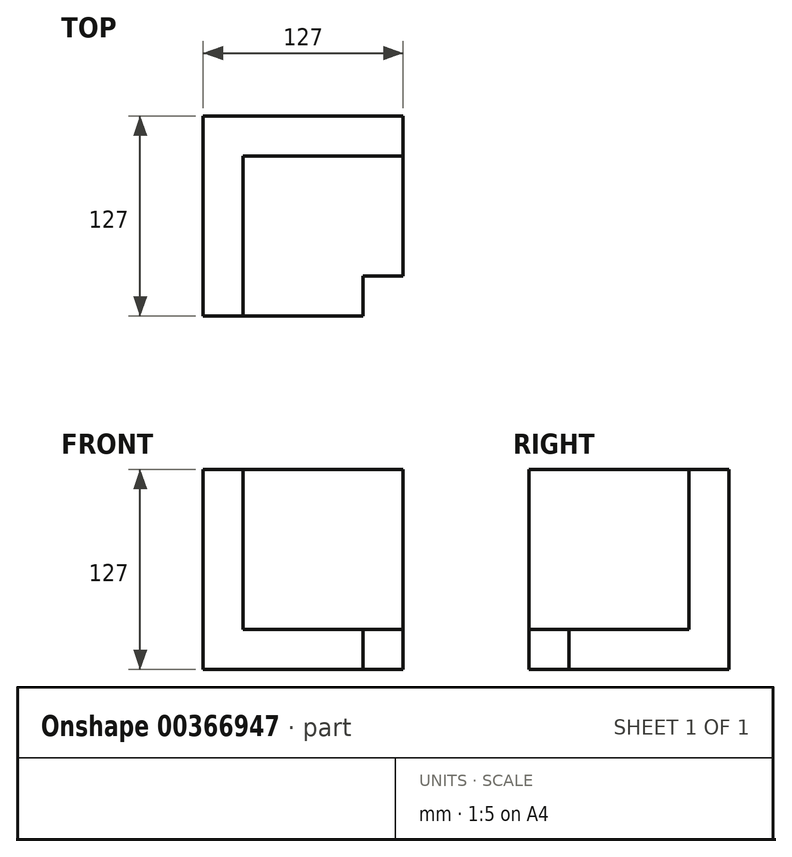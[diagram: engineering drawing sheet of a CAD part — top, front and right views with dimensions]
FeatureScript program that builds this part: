
annotation { "Feature Type Name" : "Feature", "Feature Type Description" : "" }
export const myFeature = defineFeature(function(context is Context, id is Id, definition is map)
    precondition{}
    {
        {
            var Q0;
            Q0=qCreatedBy(makeId("Top.planeOp"),FACE);
            var sketch = newSketch(context, id + "F0", { "sketchPlane" : qUnion([Q0])});
            skLineSegment(sketch, "E0.bottom", {"start": v(-56.39, 59.87) * mm, "end": v(70.61, 59.87) * mm});
            skLineSegment(sketch, "E0.top", {"start": v(-56.39, -67.13) * mm, "end": v(70.61, -67.13) * mm});
            skLineSegment(sketch, "E0.left", {"start": v(-56.39, 59.87) * mm, "end": v(-56.39, -67.13) * mm});
            skLineSegment(sketch, "E0.right", {"start": v(70.61, 59.87) * mm, "end": v(70.61, -67.13) * mm});
            skSolve(sketch);
        }
        {
            var Q0;
            Q0=makeQuery(id+"F0.imprint","IMPRINT",FACE,{"disambiguationData":[TD([[makeQuery(id+"F0.imprint","IMPRINT",EDGE,{"derivedFrom":sQuery(id+"F0.wireOp",EDGE,"E0.bottom")}),-1.0]])]});
            extrude(context, id + "F1", {"entities" : qUnion([Q0]), "depth" : 25.4 * mm});
        }
        {
            var Q0;
            Q0=makeQuery(id+"F1.opExtrude","CAP_FACE",FACE,{"disambiguationData":[OSD([sQuery(id+"F0.wireOp",EDGE,"E0.bottom"),sQuery(id+"F0.wireOp",EDGE,"E0.top"),sQuery(id+"F0.wireOp",EDGE,"E0.left"),sQuery(id+"F0.wireOp",EDGE,"E0.right")])],"isStart":false});
            var sketch = newSketch(context, id + "F2", { "sketchPlane" : qUnion([Q0])});
            skLineSegment(sketch, "E1.bottom", {"start": v(-56.39, 59.87) * mm, "end": v(-30.99, 59.87) * mm});
            skLineSegment(sketch, "E1.top", {"start": v(-56.39, -67.13) * mm, "end": v(-30.99, -67.13) * mm});
            skLineSegment(sketch, "E1.left", {"start": v(-56.39, 59.87) * mm, "end": v(-56.39, -67.13) * mm});
            skLineSegment(sketch, "E1.right", {"start": v(-30.99, 59.87) * mm, "end": v(-30.99, -67.13) * mm});
            skSolve(sketch);
        }
        {
            var Q0;
            Q0=qSketchRegion(id+"F2",true);
            var Q1;
            Q1=makeQuery(id+"F2.imprint","IMPRINT",FACE,{"disambiguationData":[TD([[makeQuery(id+"F2.imprint","IMPRINT",EDGE,{"derivedFrom":sQuery(id+"F2.wireOp",EDGE,"E1.bottom")}),-1.0]])]});
            extrude(context, id + "F3", {"entities" : qUnion([Q0, Q1]), "operationType" : NewBodyOperationType.ADD, "depth" : 101.6 * mm});
        }
        {
            var Q0;
            Q0=makeQuery(id+"F1.opExtrude","CAP_FACE",FACE,{"disambiguationData":[OSD([sQuery(id+"F0.wireOp",EDGE,"E0.bottom"),sQuery(id+"F0.wireOp",EDGE,"E0.top"),sQuery(id+"F0.wireOp",EDGE,"E0.left"),sQuery(id+"F0.wireOp",EDGE,"E0.right")])],"isStart":false});
            var sketch = newSketch(context, id + "F4", { "sketchPlane" : qUnion([Q0])});
            skLineSegment(sketch, "E2.bottom", {"start": v(-30.99, 59.87) * mm, "end": v(70.61, 59.87) * mm});
            skLineSegment(sketch, "E2.top", {"start": v(-30.99, 34.47) * mm, "end": v(70.61, 34.47) * mm});
            skLineSegment(sketch, "E2.left", {"start": v(-30.99, 59.87) * mm, "end": v(-30.99, 34.47) * mm});
            skLineSegment(sketch, "E2.right", {"start": v(70.61, 59.87) * mm, "end": v(70.61, 34.47) * mm});
            skSolve(sketch);
        }
        {
            var Q0;
            Q0=makeQuery(id+"F4.imprint","IMPRINT",FACE,{"disambiguationData":[TD([[makeQuery(id+"F4.imprint","IMPRINT",EDGE,{"derivedFrom":sQuery(id+"F4.wireOp",EDGE,"E2.bottom")}),-1.0]])]});
            extrude(context, id + "F5", {"entities" : qUnion([Q0]), "operationType" : NewBodyOperationType.ADD, "depth" : 101.6 * mm});
        }
        {
            var Q0;
            Q0=makeQuery(id+"F1.opExtrude","CAP_FACE",FACE,{"disambiguationData":[OSD([sQuery(id+"F0.wireOp",EDGE,"E0.bottom"),sQuery(id+"F0.wireOp",EDGE,"E0.top"),sQuery(id+"F0.wireOp",EDGE,"E0.left"),sQuery(id+"F0.wireOp",EDGE,"E0.right")])],"isStart":false});
            var sketch = newSketch(context, id + "F6", { "sketchPlane" : qUnion([Q0])});
            skLineSegment(sketch, "E3.bottom", {"start": v(70.61, -67.13) * mm, "end": v(45.21, -67.13) * mm});
            skLineSegment(sketch, "E3.top", {"start": v(70.61, -41.73) * mm, "end": v(45.21, -41.73) * mm});
            skLineSegment(sketch, "E3.left", {"start": v(70.61, -67.13) * mm, "end": v(70.61, -41.73) * mm});
            skLineSegment(sketch, "E3.right", {"start": v(45.21, -67.13) * mm, "end": v(45.21, -41.73) * mm});
            skSolve(sketch);
        }
        {
            var Q0;
            Q0=makeQuery(id+"F6.imprint","IMPRINT",FACE,{"disambiguationData":[TD([[makeQuery(id+"F6.imprint","IMPRINT",EDGE,{"derivedFrom":sQuery(id+"F6.wireOp",EDGE,"E3.bottom")}),1.0]])]});
            extrude(context, id + "F7", {"entities" : qUnion([Q0]), "operationType" : NewBodyOperationType.REMOVE, "oppositeDirection" : true, "depth" : 25.4 * mm});
        }
    });
